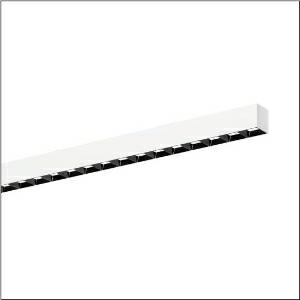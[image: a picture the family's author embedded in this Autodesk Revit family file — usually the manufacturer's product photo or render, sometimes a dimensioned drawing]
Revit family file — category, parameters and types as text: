
# Revit family: silica_r__21_51mx24da44wb_4eb4
name_source: partatom
category: Lighting Fixtures
units: mm (PartAtom-declared; Revit-internal decimal feet)

## family parameters
Cut with Voids When Loaded = No
Host = Face
Light Source = No
Part Type = Normal
Room Calculation Point = No
Round Connector Dimension = Use Diameter
Shared = No

## types (1)
- --- (1 x LED, 4320 lm, 30 W, 4000K)
    Apparent Load = 30 VA
    CIE Flux Codes = 74 94 99 100 100
    Color Rendering = 80
    Color Temperature = 4000K
    Default Elevation = 1800 mm
    Description = Silica® 21, office luminaire, primary light control with darklight reflector, of PMMA, black, CAT 2 (L<= 3000cd/m²), light emission: direct distribution, primary light characteristic: asymmetric, installation type: surface-mounted, LED, rated luminous flux: 4.320lm, luminous efficacy: 144lm/W, light colour: 840, colour temperature: 4000K, control gear: DALI 2, with terminal, 3+2-pole, max. 2.5mm², mains connection: 220..240V, AC, 50/60Hz, rated input power: 30W, luminaire housing, of aluminium, traffic white (RAL 9016), length: 1.204mm, width: 53mm, height: 53mm, protection rating (complete): IP20, insulation class (complete): insulation class I (protective earthing), certification: CE, permissible operating ambient temperature: 0..+35°C, standard: EN 50419, packaging unit: 1 piece
    Height = 53 mm
    Lamp = 1 x LED
    Lamp Light Flux = 4320 lm
    Lamp Power = 30 W
    Lamp count = 1
    Length = 1204 mm
    Luminous efficacy = 144 lm/W
    Manufacturer = Siteco
    ModVariant = No
    Model = 51MX24DA44WB
    Mounting Place = Ceiling
    Mounting Type = Surface mounted
    Number of Poles = 1
    OnlyDefault = Yes
    Power Factor = 1
    Product Name = Silica® 21
    Product group = office luminaire | ceiling mounted
    ProductGroupID = 302
    Protection Class = Protection class I
    Protection Degree = IP 20
    RLX_Detail_Level = 1
    RLX_Emergency_Light_Flux = 0 lm
    RLX_Emergency_Type = 0
    RLX_Emergency_Type_DB = No
    RlxData = <blob elided: 41501 chars, md5=f53b8e79>
    Socket = socket
    Standby Power = 0 W
    System Light Flux = 4320 lm
    System Power = 30 W
    Type Comments = factory setting: luminous flux: 100 % | dim-lin: 254 | 418 mA
    Type Image = l_1335873.jpg
    URL = http://relux.com
    VarID = @adj_123286
    Voltage = 0 V
    Weight = 0.00 kg
    Width = 53 mm

## geometry (parser evidence)
native form markers: Blend x4, Sweep x10
no freeform markers — native parametric forms only
